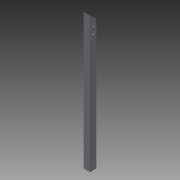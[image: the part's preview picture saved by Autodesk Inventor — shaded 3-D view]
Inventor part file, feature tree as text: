
AUTODESK INVENTOR PART (.ipt)
format: ipt  version: 2013 (Build 170138000, 138)  size: 105,472 bytes
history: native  units: in
note: dims shown in document units (in); Inventor stores cm internally (conversion verified against a paired STEP export)
features: extrude x4, sketch x4
ambient origin geometry x8: Origin, YZ Plane, XZ Plane, XY Plane, X Axis, Y Axis, Z Axis, Center Point
bodies: Solid1 (feature_tree)
feature tree (8):
  extrude  "Extrusion1"  Depth=1.0in
  extrude  "Extrusion2"  Depth=0.75in
  extrude  "Extrusion3"  TaperAngle=45.0deg  [1 undecoded]
  extrude  "Extrusion4"  Depth=0.701in
  sketch  "Sketch1"  dims[d0=1.0in d1=1.0in]
  sketch  "Sketch2"  dims[d2=0.75in d3=0.75in]
  sketch  "Sketch3"  dims[d4=21.0in d5=0.0in d6=45.0deg]
  sketch  "Sketch4"  dims[d7=1.0in d8=0.0in d9=0.701in d10=0.2in d11=1.0in d12=0.0in d13=18.257in d14=90.0deg d15=1.0in d16=180.0deg d17=0.25in d18=0.25in d19=1.0in d20=0.0in]
note: 1 required parameter value undecoded (feature->parameter linkage not recoverable at this tier; creation-order binding heuristic only, values carry confidence <= 0.55)
